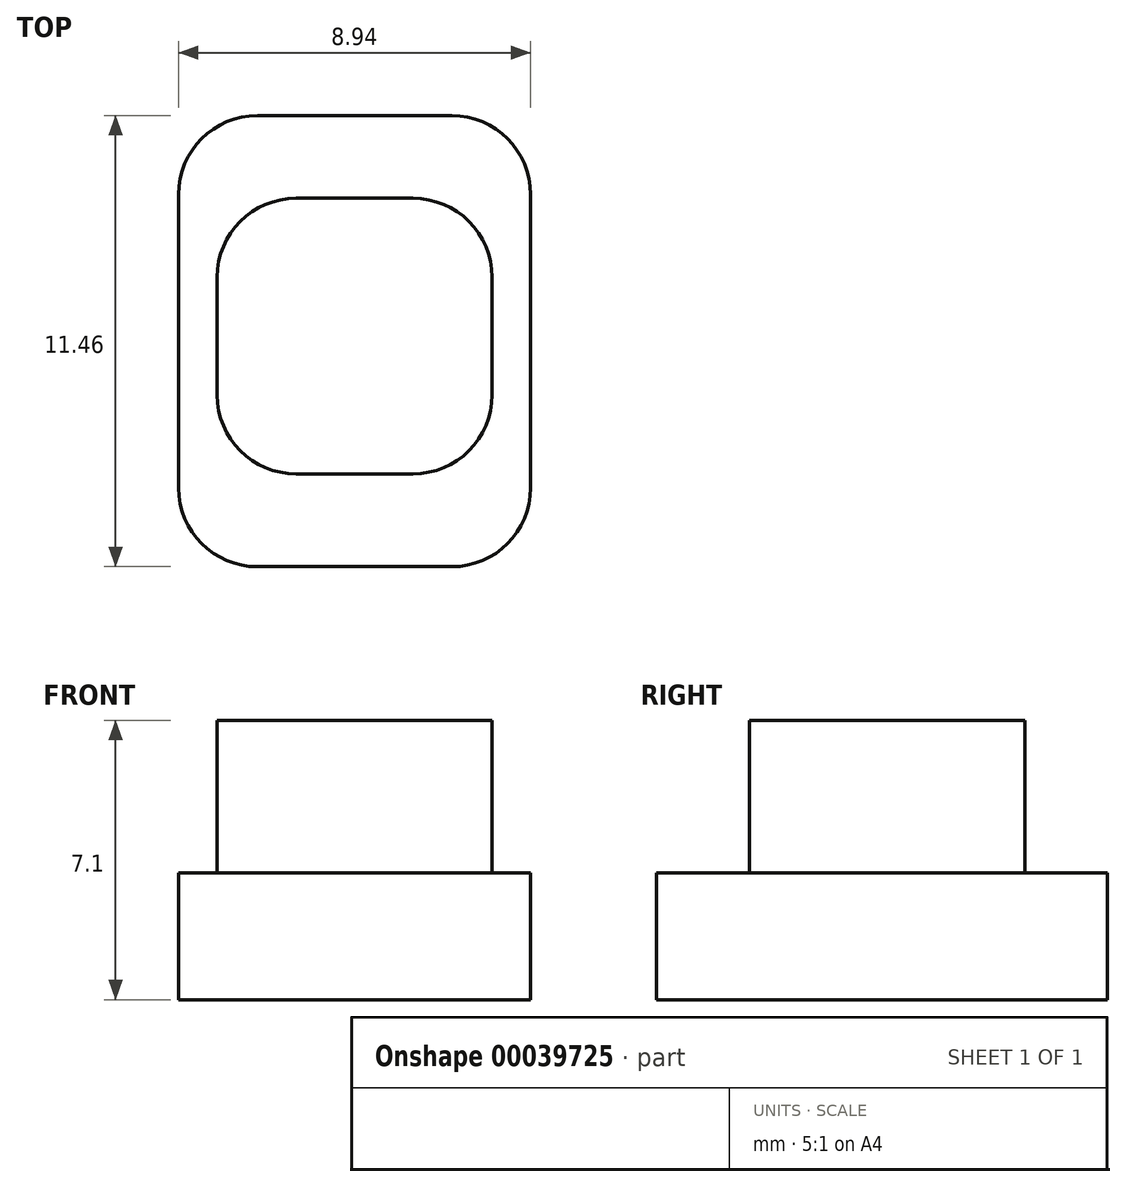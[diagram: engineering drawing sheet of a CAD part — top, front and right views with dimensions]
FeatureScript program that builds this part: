
annotation { "Feature Type Name" : "Feature", "Feature Type Description" : "" }
export const myFeature = defineFeature(function(context is Context, id is Id, definition is map)
    precondition{}
    {
        {
            var Q0;
            Q0=qCreatedBy(makeId("Top.planeOp"),FACE);
            var sketch = newSketch(context, id + "F0", { "sketchPlane" : qUnion([Q0])});
            skLineSegment(sketch, "E0.bottom", {"start": v(0, 0) * mm, "end": v(8.94, 0) * mm});
            skLineSegment(sketch, "E0.top", {"start": v(0, -11.46) * mm, "end": v(8.94, -11.46) * mm});
            skLineSegment(sketch, "E0.left", {"start": v(0, 0) * mm, "end": v(0, -11.46) * mm});
            skLineSegment(sketch, "E0.right", {"start": v(8.94, 0) * mm, "end": v(8.94, -11.46) * mm});
            skLineSegment(sketch, "E1.bottom", {"start": v(0.98, -2.1) * mm, "end": v(7.96, -2.1) * mm});
            skLineSegment(sketch, "E1.top", {"start": v(0.98, -9.1) * mm, "end": v(7.96, -9.1) * mm});
            skLineSegment(sketch, "E1.left", {"start": v(0.98, -2.1) * mm, "end": v(0.98, -9.1) * mm});
            skLineSegment(sketch, "E1.right", {"start": v(7.96, -2.1) * mm, "end": v(7.96, -9.1) * mm});
            skPoint(sketch, "E2", {"position": v(4.47, -2.1) * mm});
            skPoint(sketch, "E3", {"position": v(4.47, 0) * mm});
            skSolve(sketch);
        }
        {
            var Q0;
            Q0=makeQuery(id+"F0.imprint","IMPRINT",FACE,{"disambiguationData":[TD([[makeQuery(id+"F0.imprint","IMPRINT",EDGE,{"derivedFrom":sQuery(id+"F0.wireOp",EDGE,"E0.bottom")}),-1.0]])]});
            extrude(context, id + "F1", {"entities" : qUnion([Q0]), "depth" : 3.22 * mm});
        }
        {
            var Q0;
            Q0=makeQuery(id+"F0.imprint","IMPRINT",FACE,{"disambiguationData":[TD([[makeQuery(id+"F0.imprint","IMPRINT",EDGE,{"derivedFrom":sQuery(id+"F0.wireOp",EDGE,"E1.bottom")}),-1.0]])]});
            extrude(context, id + "F2", {"entities" : qUnion([Q0]), "operationType" : NewBodyOperationType.ADD, "depth" : 7.1 * mm});
        }
        {
            var Q0;
            Q0=makeQuery(id+"F2.opExtrude","SWEPT_EDGE",EDGE,{"disambiguationData":[OSD([sQuery(id+"F0.wireOp",EDGE,"E1.top"),sQuery(id+"F0.wireOp",EDGE,"E1.left")])]});
            var Q1;
            Q1=makeQuery(id+"F2.opExtrude","SWEPT_EDGE",EDGE,{"disambiguationData":[OSD([sQuery(id+"F0.wireOp",EDGE,"E1.top"),sQuery(id+"F0.wireOp",EDGE,"E1.right")])]});
            var Q2;
            Q2=makeQuery(id+"F2.opExtrude","SWEPT_EDGE",EDGE,{"disambiguationData":[OSD([sQuery(id+"F0.wireOp",EDGE,"E1.bottom"),sQuery(id+"F0.wireOp",EDGE,"E1.right")])]});
            var Q3;
            Q3=makeQuery(id+"F2.opExtrude","SWEPT_EDGE",EDGE,{"disambiguationData":[OSD([sQuery(id+"F0.wireOp",EDGE,"E1.bottom"),sQuery(id+"F0.wireOp",EDGE,"E1.left")])]});
            var Q4;
            Q4=makeQuery(id+"F1.opExtrude","SWEPT_EDGE",EDGE,{"disambiguationData":[OSD([sQuery(id+"F0.wireOp",EDGE,"E0.top"),sQuery(id+"F0.wireOp",EDGE,"E0.right")])]});
            var Q5;
            Q5=makeQuery(id+"F1.opExtrude","SWEPT_EDGE",EDGE,{"disambiguationData":[OSD([sQuery(id+"F0.wireOp",EDGE,"E0.bottom"),sQuery(id+"F0.wireOp",EDGE,"E0.right")])]});
            var Q6;
            Q6=makeQuery(id+"F1.opExtrude","SWEPT_EDGE",EDGE,{"disambiguationData":[OSD([sQuery(id+"F0.wireOp",EDGE,"E0.bottom"),sQuery(id+"F0.wireOp",EDGE,"E0.left")])]});
            var Q7;
            Q7=makeQuery(id+"F1.opExtrude","SWEPT_EDGE",EDGE,{"disambiguationData":[OSD([sQuery(id+"F0.wireOp",EDGE,"E0.top"),sQuery(id+"F0.wireOp",EDGE,"E0.left")])]});
            fillet(context, id + "F3", {"entities" : qUnion([Q0, Q1, Q2, Q3, Q4, Q5, Q6, Q7]), "radius" : 2 * mm, "allowEdgeOverflow" : false});
        }
    });
